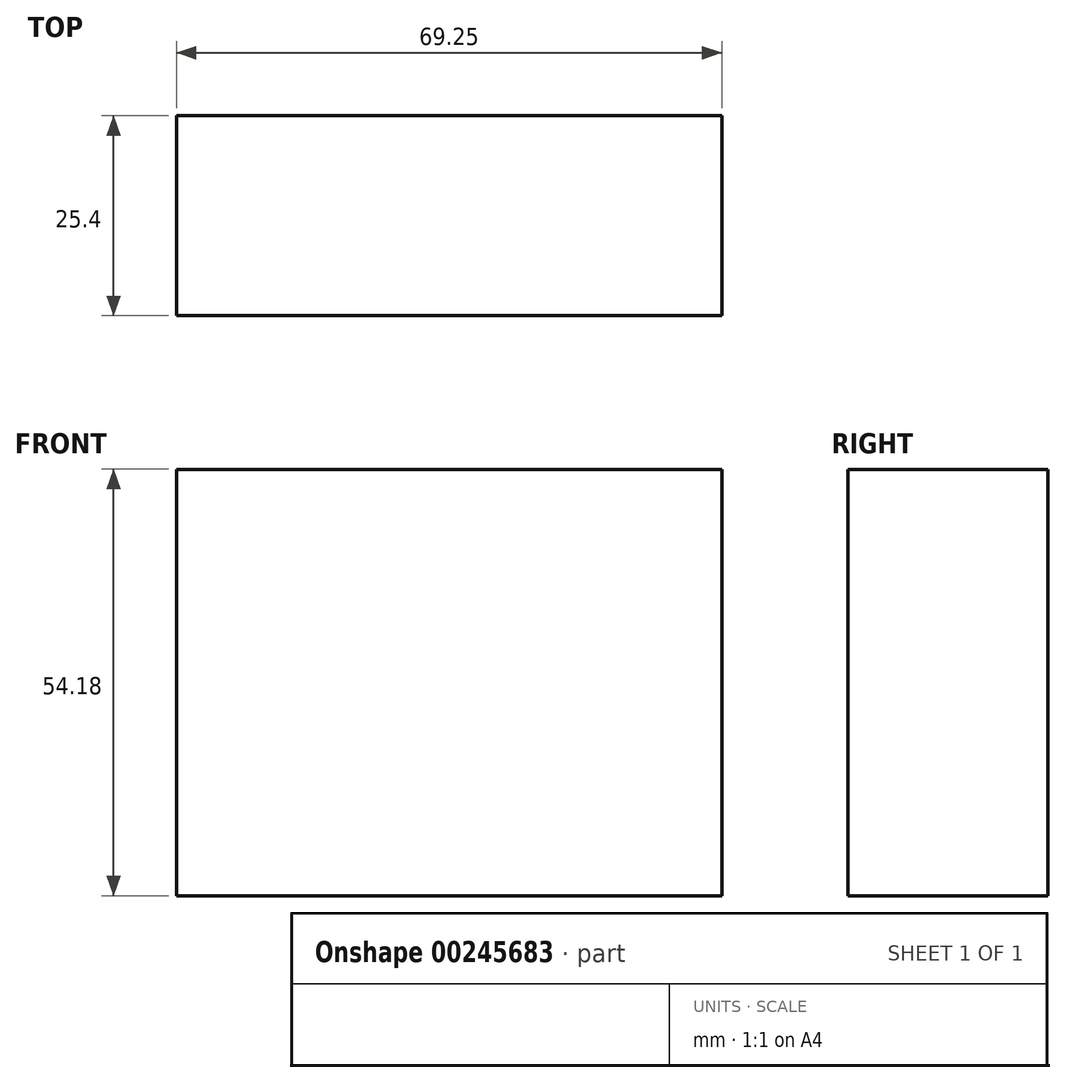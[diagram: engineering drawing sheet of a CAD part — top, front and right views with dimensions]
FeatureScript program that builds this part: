
annotation { "Feature Type Name" : "Feature", "Feature Type Description" : "" }
export const myFeature = defineFeature(function(context is Context, id is Id, definition is map)
    precondition{}
    {
        {
            var Q0;
            Q0=qCreatedBy(makeId("Front.planeOp"),FACE);
            var sketch = newSketch(context, id + "F1", { "sketchPlane" : qUnion([Q0])});
            skLineSegment(sketch, "E0.bottom", {"start": v(-26.92, 28.47) * mm, "end": v(42.33, 28.47) * mm});
            skLineSegment(sketch, "E0.top", {"start": v(-26.92, -25.71) * mm, "end": v(42.33, -25.71) * mm});
            skLineSegment(sketch, "E0.left", {"start": v(-26.92, 28.47) * mm, "end": v(-26.92, -25.71) * mm});
            skLineSegment(sketch, "E0.right", {"start": v(42.33, 28.47) * mm, "end": v(42.33, -25.71) * mm});
            skSolve(sketch);
        }
        {
            var Q0;
            Q0 = qSketchRegion(id + "F1", true);
            extrude(context, id + "F0", {"entities" : qUnion([Q0]), "depth" : 25.4 * mm});
        }
    });
